# Revit family: Hager-MINIGAMMA-Surface_mounted-IP30-Without_Cover-With_DIN-NoHosted-FR-fr
name_source: partatom
category: Electrical Equipment
units: mm (PartAtom-declared; Revit-internal decimal feet)

## family parameters
Always vertical = Yes
Cut with Voids When Loaded = No
Maintain Annotation Orientation = No
Panel Configuration = Two Columns, Circuits Across
Part Type = Panelboard
Room Calculation Point = No
Round Connector Dimension = Use Diameter
Shared = No
Work Plane-Based = Yes

## types (2) — shared parameters
BC_METADATA = {"ObjectGuid":"bc35c96e-cb38-443e-833d-0616858cb9ac","ModelGuid":"8af03f69-2293-4735-a617-cc53adf55621","VariantGuid":"8b6e323b-1b53-409a-a940-11b5a7fc5337","Revision":"#4","VariantName":"Template-Enclosure_EU-EC000214"}
BC_MODEL_ID = 1554402
BC_OBJECT_ID = 513903
BC_OBJECT_VERSION = #5
Code hager = ADD-EC000214_EU
Default Elevation = 1200 mm
EF000003 - mode de pose = saillie
EF000024 - résistant aux UV = No
EF000049 - profondeur = 82 mm  [stored 0.269029 ft]
EF000116 - numéro RAL = 9010
EF000118 - avec cadre/support de montage = No
EF000266 - nombre de rangées = 1
EF001062 - finition CEM = No
EF001134 - rail DIN = Yes
EF005474 - indice de protection (IP) = IP30
EF006244 - couvercle/porte transparent(e) = No
EF006306 - avec serrure = No
EF015776 - borne de mise à la terre = No
EF015777 - borne à conducteur neutre = No
EF015941 - porte pour transmission du signal = No
ETIM class code = EC000214
ETIM class name = Small distribution board
HG000001-nombre de colonnes = 1
HG000002-avec porte = No
HG000003-Gamme = MINIGAMMA
HG000005-Epaisseur = 2 mm  [stored 0.00656168 ft]
HG000006-Encastré = No
HG000009-Porte à double battant = No
HG000010-Portes asymétriques = No
HG000011-Rangées du bas vides = No
HG000012-Angle de pivotement de la porte = 90.00°
HG000013-Porte à gauche = No
HG000014-Porte à droite = Yes
HG000015-Visibilité de l'emprise de la porte = Yes
HG000016-Visibilité de la porte 3D = Yes
HG000017-Distance entre pôles = 18 mm  [stored 0.0590551 ft]
HG000060-RAL-number = 9010
HG000099-ID modèle Onfly = 507532
HGEF000266-Nombre de rangées = 1
Manufacturer = Hager
Name = MINIGAMMA-Surface_mounted-IP30-Without_Cover-With_DIN-FR
Name BIM&CO = Electricity
Name hager = ADD_Enclosures_EC000214
Uniformat = Low Tension Service & Dist.
Uniformat code = D501001
zero-valued in all types: EF000218 - profondeur d'encastrement, EF000332 - hauteur d'encastrement, EF000846 - largeur d'encastrement, EF001131 - profondeur intérieure, HG000007-Nombre de colonnes vides, HG000008-Nombre de rangées vides

## per-type parameters (varying)
| type | BC_VARIANT_ID | EF000007 - couleur | EF000008 - largeur | EF000040 - hauteur | EF001088 - possibilité de montage en saillie | EF002950 - largeur en nombre de modules | EF004462 - type de fermeture | EF009212 - finition du couvercle | HG000004-Référence fabricant | HGEF0002950-largeur en nombre de modules |
| MINIGAMMA-Surface_mounted_W55_H160_D82_2_Modular_Spacing-GD102A | 1179058 | blanc | 55 mm  [stored 0.180446 ft] | 160 mm | Yes | 2 | autre | avec échancrure | GD102A | 2 |
| MINIGAMMA-Surface_mounted_W182_H180_D82_8_Modular_Spacing-GD108E | 1179059 |  | 182 mm  [stored 0.597113 ft] | 180 mm  [stored 0.590551 ft] | No | 8 |  |  | GD108E | 8 |

note: column(s) folded — value = type name in every type: Reference

note: [stored X ft] marks values corroborated as IEEE doubles in the binary element streams (Revit-internal decimal feet)

## geometry (parser evidence)
native form markers: Sweep x14
no freeform markers — native parametric forms only
